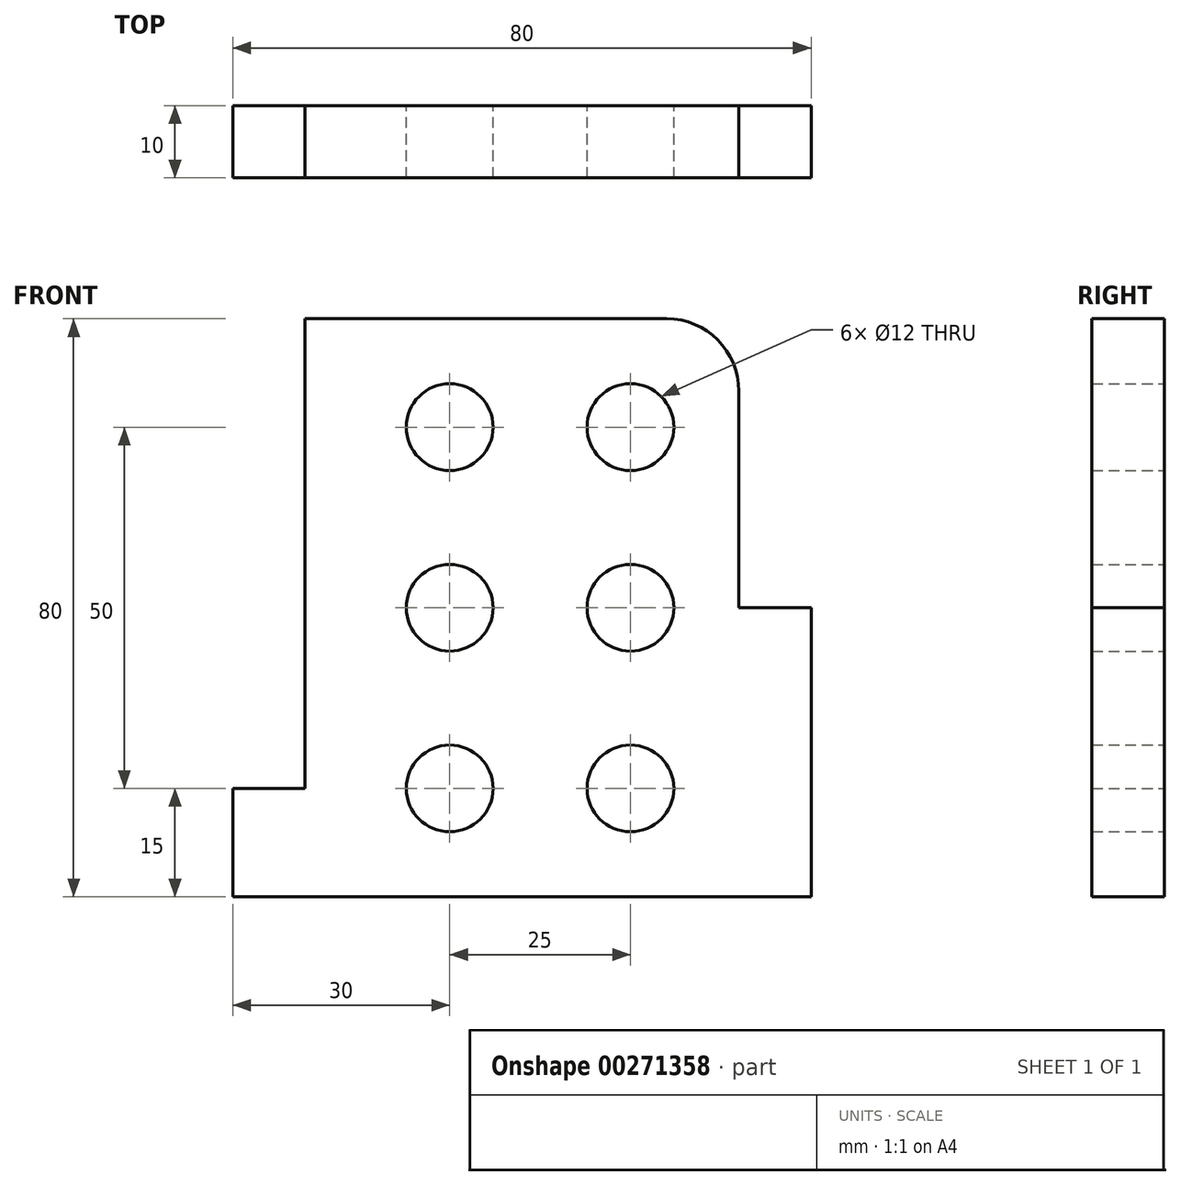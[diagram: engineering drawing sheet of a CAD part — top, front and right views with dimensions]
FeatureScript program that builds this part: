
annotation { "Feature Type Name" : "Feature", "Feature Type Description" : "" }
export const myFeature = defineFeature(function(context is Context, id is Id, definition is map)
    precondition{}
    {
        {
            var Q0;
            Q0=qCreatedBy(makeId("Front.planeOp"),FACE);
            var sketch = newSketch(context, id + "F0", { "sketchPlane" : qUnion([Q0])});
            skLineSegment(sketch, "E0", {"start": v(0, 0) * mm, "end": v(80, 0) * mm});
            skLineSegment(sketch, "E1", {"start": v(80, 0) * mm, "end": v(80, 40) * mm});
            skLineSegment(sketch, "E2", {"start": v(80, 40) * mm, "end": v(70, 40) * mm});
            skLineSegment(sketch, "E3", {"start": v(0, 0) * mm, "end": v(0, 15) * mm});
            skLineSegment(sketch, "E4", {"start": v(0, 15) * mm, "end": v(10, 15) * mm});
            skLineSegment(sketch, "E5", {"start": v(10, 15) * mm, "end": v(10, 80) * mm});
            skCircle(sketch, "E6", {"center": v(55, 15) * mm, "radius": 6 * mm});
            skCircle(sketch, "E7", {"center": v(30, 15) * mm, "radius": 6 * mm});
            skCircle(sketch, "E8", {"center": v(55, 40) * mm, "radius": 6 * mm});
            skCircle(sketch, "E9", {"center": v(30, 40) * mm, "radius": 6 * mm});
            skCircle(sketch, "E10", {"center": v(30, 65) * mm, "radius": 6 * mm});
            skCircle(sketch, "E11", {"center": v(55, 65) * mm, "radius": 6 * mm});
            skLineSegment(sketch, "E12", {"start": v(70, 70) * mm, "end": v(70, 40) * mm});
            skLineSegment(sketch, "E13", {"start": v(60, 80) * mm, "end": v(10, 80) * mm});
            skArc(sketch, "E14", {"start": v(70, 70) * mm, "mid": v(67.07, 77.07) * mm, "end": v(60, 80) * mm});
            skSolve(sketch);
        }
        {
            var Q0;
            Q0=makeQuery(id+"F0.imprint","IMPRINT",FACE,{"disambiguationData":[TD([[makeQuery(id+"F0.imprint","IMPRINT",EDGE,{"derivedFrom":sQuery(id+"F0.wireOp",EDGE,"E0")}),1.0]])]});
            extrude(context, id + "F1", {"entities" : qUnion([Q0]), "depth" : 10 * mm});
        }
    });
